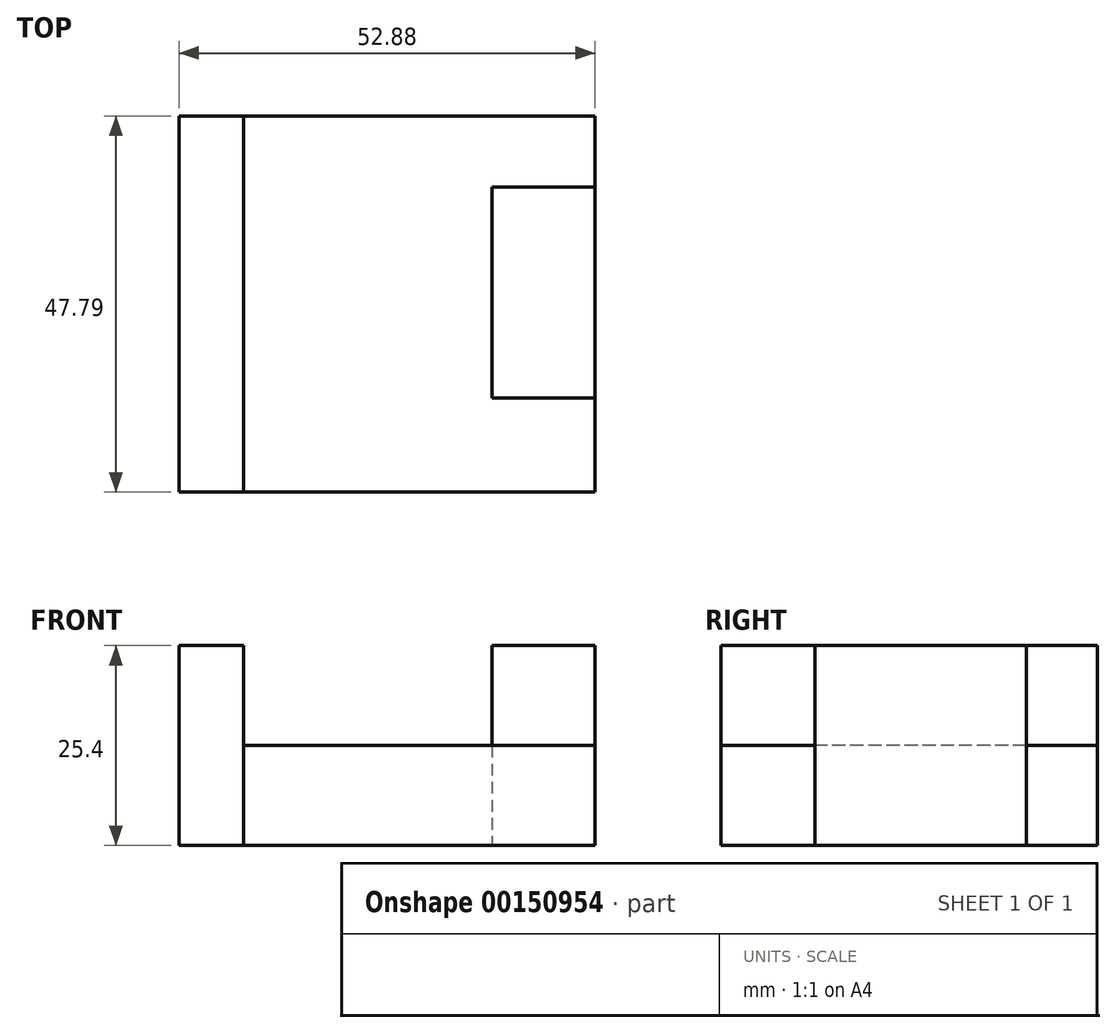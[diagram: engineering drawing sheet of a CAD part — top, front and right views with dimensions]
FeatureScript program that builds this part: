
annotation { "Feature Type Name" : "Feature", "Feature Type Description" : "" }
export const myFeature = defineFeature(function(context is Context, id is Id, definition is map)
    precondition{}
    {
        {
            var Q0;
            Q0=qCreatedBy(makeId("Top.planeOp"),FACE);
            var sketch = newSketch(context, id + "F0", { "sketchPlane" : qUnion([Q0])});
            skLineSegment(sketch, "E0.bottom", {"start": v(-41.72, 62.38) * mm, "end": v(11.16, 62.38) * mm});
            skLineSegment(sketch, "E0.top", {"start": v(-41.72, 14.6) * mm, "end": v(11.16, 14.6) * mm});
            skLineSegment(sketch, "E0.left", {"start": v(-41.72, 62.38) * mm, "end": v(-41.72, 14.6) * mm});
            skLineSegment(sketch, "E0.right", {"start": v(11.16, 62.38) * mm, "end": v(11.16, 14.6) * mm});
            skLineSegment(sketch, "E1", {"start": v(11.16, 53.37) * mm, "end": v(-1.96, 53.37) * mm});
            skLineSegment(sketch, "E2", {"start": v(-1.96, 53.37) * mm, "end": v(-1.96, 26.54) * mm});
            skLineSegment(sketch, "E3", {"start": v(-1.96, 26.54) * mm, "end": v(11.16, 26.54) * mm});
            skLineSegment(sketch, "E4", {"start": v(-33.5, 62.38) * mm, "end": v(-33.5, 14.6) * mm});
            skSolve(sketch);
        }
        {
            var Q0;
            {var subQ0=sQuery(id+"F0.wireOp",EDGE,"E0.left");Q0=makeQuery(id+"F0.imprint","IMPRINT",FACE,{"disambiguationData":[TD([[makeQuery(id+"F0.imprint","IMPRINT",EDGE,{"derivedFrom":subQ0}),1.0]])]});}
            var Q1;
            {var subQ0=sQuery(id+"F0.wireOp",EDGE,"E1");Q1=makeQuery(id+"F0.imprint","IMPRINT",FACE,{"disambiguationData":[TD([[makeQuery(id+"F0.imprint","IMPRINT",EDGE,{"derivedFrom":subQ0}),1.0]])]});}
            extrude(context, id + "F1", {"entities" : qUnion([Q0, Q1]), "depth" : 25.4 * mm});
        }
        {
            var Q0;
            {var subQ6=sQuery(id+"F0.wireOp",EDGE,"E1");Q0=makeQuery(id+"F0.imprint","IMPRINT",FACE,{"disambiguationData":[TD([[makeQuery(id+"F0.imprint","IMPRINT",EDGE,{"derivedFrom":subQ6}),-1.0]])]});}
            extrude(context, id + "F2", {"entities" : qUnion([Q0]), "depth" : 12.7 * mm});
        }
    });
